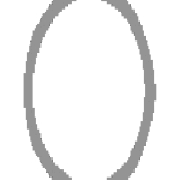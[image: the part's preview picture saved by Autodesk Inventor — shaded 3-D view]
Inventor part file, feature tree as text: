
AUTODESK INVENTOR PART (.ipt)
format: ipt  version: 2021 (Build 250183000, 183)  size: 112,640 bytes
history: native  units: in
note: dims shown in document units (in); Inventor stores cm internally (conversion verified against a paired STEP export)
features: other x4, sketch x3, plane x1
ambient origin geometry x8: Origin, YZ Plane, XZ Plane, XY Plane, X Axis, Y Axis, Z Axis, Center Point
bodies: Solid1 (feature_tree), Body (feature_tree)
feature tree (8):
  other  "Driven Length"
  other  "Frame Generator"
  other  "Start Plane"
  other  "End Plane"
  sketch  "Sketch"  dims[d2=4.559in d4=-0.0in d5=4.559in d6=0.12in d7=0.0in d8=90.0deg d9=4.559in]
  sketch  "Sketch2"  dims[d0=1.0in]
  plane  "Work Plane3"
  sketch  "Sketch3"  dims[d1=0.065in]
